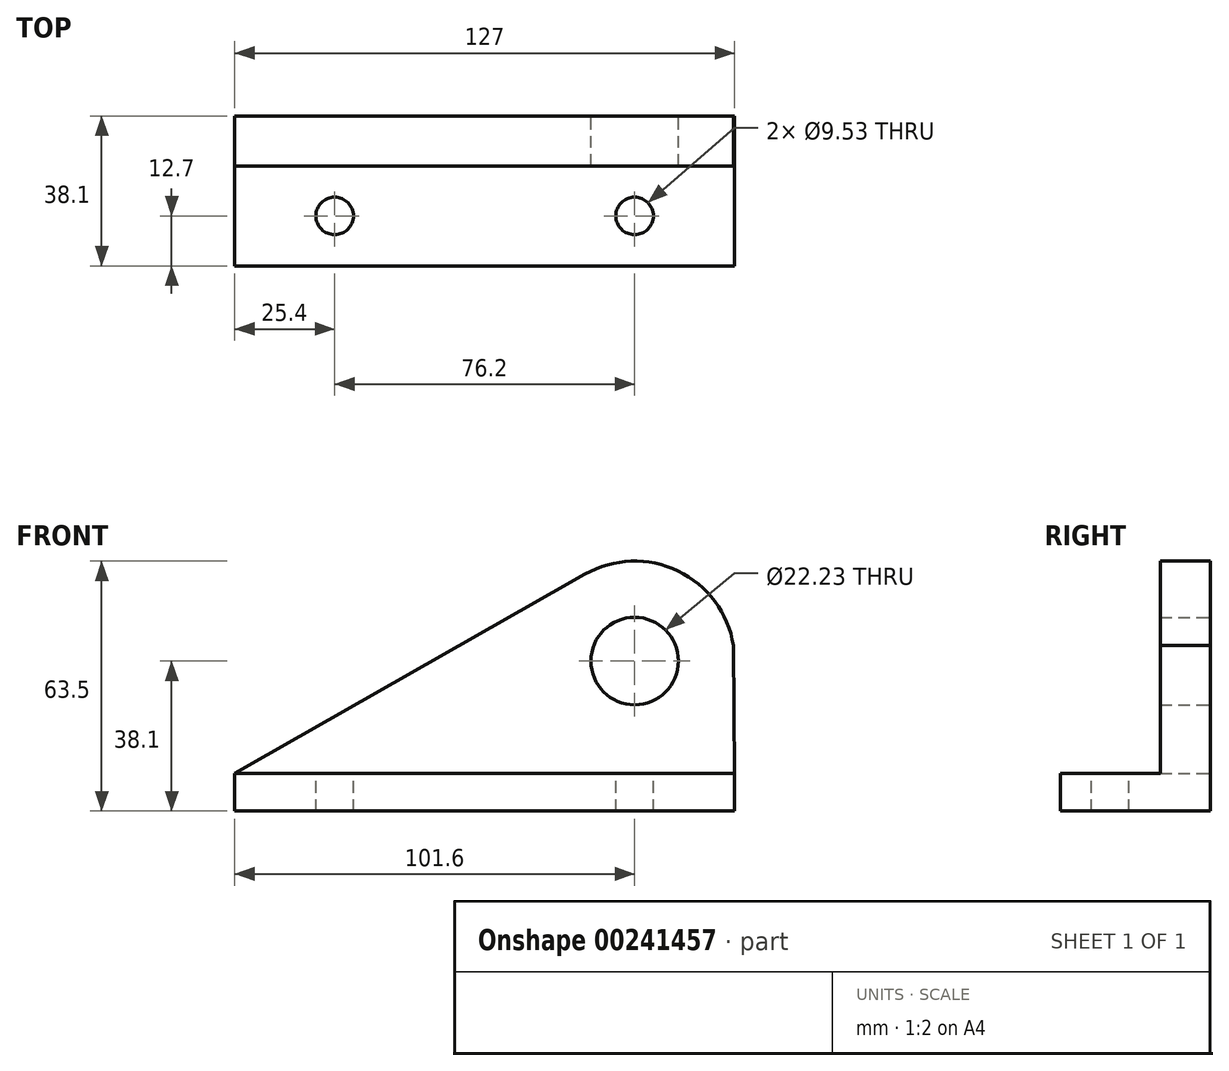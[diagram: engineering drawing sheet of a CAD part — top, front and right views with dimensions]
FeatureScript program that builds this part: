
annotation { "Feature Type Name" : "Feature", "Feature Type Description" : "" }
export const myFeature = defineFeature(function(context is Context, id is Id, definition is map)
    precondition{}
    {
        {
            var Q0;
            Q0=qCreatedBy(makeId("Front.planeOp"),FACE);
            var sketch = newSketch(context, id + "F0", { "sketchPlane" : qUnion([Q0])});
            skLineSegment(sketch, "E0", {"start": v(0, 0) * mm, "end": v(127, 0) * mm});
            skLineSegment(sketch, "E1", {"start": v(127, 0) * mm, "end": v(127, 9.52) * mm});
            skLineSegment(sketch, "E2", {"start": v(127, 9.52) * mm, "end": v(0, 9.52) * mm});
            skLineSegment(sketch, "E3", {"start": v(0, 9.52) * mm, "end": v(0, 0) * mm});
            skLineSegment(sketch, "E4", {"start": v(127, 9.52) * mm, "end": v(101.6, 9.52) * mm});
            skArc(sketch, "E5", {"start": v(126.76, 34.61) * mm, "mid": v(115.85, 59.13) * mm, "end": v(89.04, 60.18) * mm});
            skLineSegment(sketch, "E6", {"start": v(127, 9.52) * mm, "end": v(126.69, 42.07) * mm});
            skLineSegment(sketch, "E7", {"start": v(0, 9.52) * mm, "end": v(89.04, 60.18) * mm});
            skSolve(sketch);
        }
        {
            var Q0;
            Q0=makeQuery(id+"F0.imprint","IMPRINT",FACE,{"disambiguationData":[TD([[makeQuery(id+"F0.imprint","IMPRINT",EDGE,{"derivedFrom":sQuery(id+"F0.wireOp",EDGE,"E0")}),1.0]])]});
            extrude(context, id + "F1", {"entities" : qUnion([Q0]), "depth" : 38.1 * mm});
        }
        {
            var Q0;
            Q0=makeQuery(id+"F0.imprint","IMPRINT",FACE,{"disambiguationData":[TD([[makeQuery(id+"F0.imprint","IMPRINT",EDGE,{"derivedFrom":sQuery(id+"F0.wireOp",EDGE,"E2")}),-1.0]])]});
            extrude(context, id + "F2", {"entities" : qUnion([Q0]), "operationType" : NewBodyOperationType.ADD, "depth" : 12.7 * mm});
        }
        {
            var Q0;
            Q0=sQuery(id+"F0.wireOp",VERTEX,"E5.center");
            var Q1;
            Q1=makeQuery(id+"F1.opExtrude","SWEPT_BODY",BODY,{"disambiguationData":[OSD([sQuery(id+"F0.wireOp",EDGE,"E0"),sQuery(id+"F0.wireOp",EDGE,"E1"),sQuery(id+"F0.wireOp",EDGE,"E2"),sQuery(id+"F0.wireOp",EDGE,"E3"),sQuery(id+"F0.wireOp",EDGE,"E4")])]});
            hole(context, id + "F3", {"style" : HoleStyle.SIMPLE, "endStyle" : HoleEndStyle.THROUGH, "oppositeDirection" : true, "holeDiameter" : 22.22 * mm, "locations" : qUnion([Q0]), "scope" : qUnion([Q1]), "isTappedThrough" : true});
        }
        {
            var Q0;
            Q0=makeQuery(id+"F1.opExtrude","SWEPT_FACE",FACE,{"disambiguationData":[OSD([sQuery(id+"F0.wireOp",EDGE,"E2"),sQuery(id+"F0.wireOp",EDGE,"E4")])]});
            var sketch = newSketch(context, id + "F4", { "sketchPlane" : qUnion([Q0])});
            skLineSegment(sketch, "E8", {"start": v(0, -38.1) * mm, "end": v(0, -25.4) * mm});
            skPoint(sketch, "E9.end.orphan", {"position": v(127, -25.4) * mm});
            skCircle(sketch, "E10", {"center": v(25.4, -25.4) * mm, "radius": 4.76 * mm});
            skCircle(sketch, "E11", {"center": v(101.6, -25.4) * mm, "radius": 4.76 * mm});
            skSolve(sketch);
        }
        {
            var Q0;
            Q0=sQuery(id+"F4.wireOp",VERTEX,"E10.center");
            var Q1;
            Q1=makeQuery(id+"F1.opExtrude","SWEPT_BODY",BODY,{"disambiguationData":[OSD([sQuery(id+"F0.wireOp",EDGE,"E0"),sQuery(id+"F0.wireOp",EDGE,"E1"),sQuery(id+"F0.wireOp",EDGE,"E2"),sQuery(id+"F0.wireOp",EDGE,"E3"),sQuery(id+"F0.wireOp",EDGE,"E4")])]});
            hole(context, id + "F5", {"style" : HoleStyle.SIMPLE, "endStyle" : HoleEndStyle.THROUGH, "holeDiameter" : 9.52 * mm, "locations" : qUnion([Q0]), "scope" : qUnion([Q1]), "isTappedThrough" : true});
        }
        {
            var Q0;
            Q0=sQuery(id+"F4.wireOp",VERTEX,"E11.center");
            var Q1;
            Q1=makeQuery(id+"F1.opExtrude","SWEPT_BODY",BODY,{"disambiguationData":[OSD([sQuery(id+"F0.wireOp",EDGE,"E0"),sQuery(id+"F0.wireOp",EDGE,"E1"),sQuery(id+"F0.wireOp",EDGE,"E2"),sQuery(id+"F0.wireOp",EDGE,"E3"),sQuery(id+"F0.wireOp",EDGE,"E4")])]});
            hole(context, id + "F6", {"style" : HoleStyle.SIMPLE, "endStyle" : HoleEndStyle.THROUGH, "holeDiameter" : 9.52 * mm, "locations" : qUnion([Q0]), "scope" : qUnion([Q1]), "isTappedThrough" : true});
        }
    });
